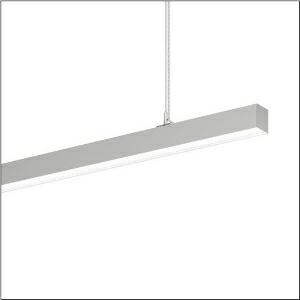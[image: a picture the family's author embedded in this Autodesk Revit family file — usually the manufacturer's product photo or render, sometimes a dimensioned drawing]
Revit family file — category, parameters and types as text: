
# Revit family: silica_r__21_51mx33dc3dsb_c168
name_source: partatom
category: Lighting Fixtures
units: mm (PartAtom-declared; Revit-internal decimal feet)

## family parameters
Cut with Voids When Loaded = No
Host = Face
Light Source = No
Part Type = Normal
Room Calculation Point = No
Round Connector Dimension = Use Diameter
Shared = No

## types (1)
- --- (1 x LED, 14780 lm, 99.5 W, 3000K)
    Apparent Load = 100 VA
    CIE Flux Codes = 78 96 99 55 100
    Color Rendering = 80
    Color Temperature = 3000K
    Default Elevation = 1800 mm
    Description = Silica® 21, office luminaire, primary optical cover: prismatic diffuser, of PMMA, CAT 2 (L<= 3000cd/m²), light emission: direct/indirect distribution, primary light characteristic: symmetric, installation type: suspended mounting, LED, rated luminous flux: 14.780lm, luminous efficacy: 149lm/W, light colour: 830, colour temperature: 3000K, control gear: DALI 2, with terminal, 3+2-pole, max. 2.5mm², mains connection: 220..240V, AC, 50/60Hz, rated input power: 99.5W, luminaire housing, of aluminium, metallic grey (RAL 9006), length: 3.004mm, width: 53mm, height: 53mm, protection rating (complete): IP20, insulation class (complete): insulation class I (protective earthing), certification: CE, permissible operating ambient temperature: 0..+35°C, standard: EN 50419, packaging unit: 1 piece
    Height = 53 mm
    Lamp = 1 x LED
    Lamp Light Flux = 14780 lm
    Lamp Power = 99.5 W
    Lamp count = 1
    Length = 3004 mm
    Luminous efficacy = 149 lm/W
    Manufacturer = Siteco
    ModVariant = No
    Model = 51MX33DC3DSB
    Mounting Place = Ceiling
    Mounting Type = Pendant
    Number of Poles = 1
    OnlyDefault = Yes
    Power Factor = 1
    Product Name = Silica® 21
    Product group = office luminaire | ceiling pendant
    ProductGroupID = 904
    Protection Class = Protection class I
    Protection Degree = IP 20
    RLX_Detail_Level = 1
    RLX_Emergency_Light_Flux = 0 lm
    RLX_Emergency_Type = 0
    RLX_Emergency_Type_DB = No
    RlxData = <blob elided: 23501 chars, md5=8e650e11>
    Socket = socket
    Standby Power = 0 W
    System Light Flux = 14780 lm
    System Power = 100 W
    Type Comments = factory setting: luminous flux: 100 % | dim-lin: 254 | 345 mA
    Type Image = l_1335864.jpg
    URL = http://relux.com
    VarID = @adj_118462
    Voltage = 0 V
    Weight = 0.00 kg
    Width = 53 mm

## geometry (parser evidence)
native form markers: Blend x4, Sweep x16
no freeform markers — native parametric forms only
